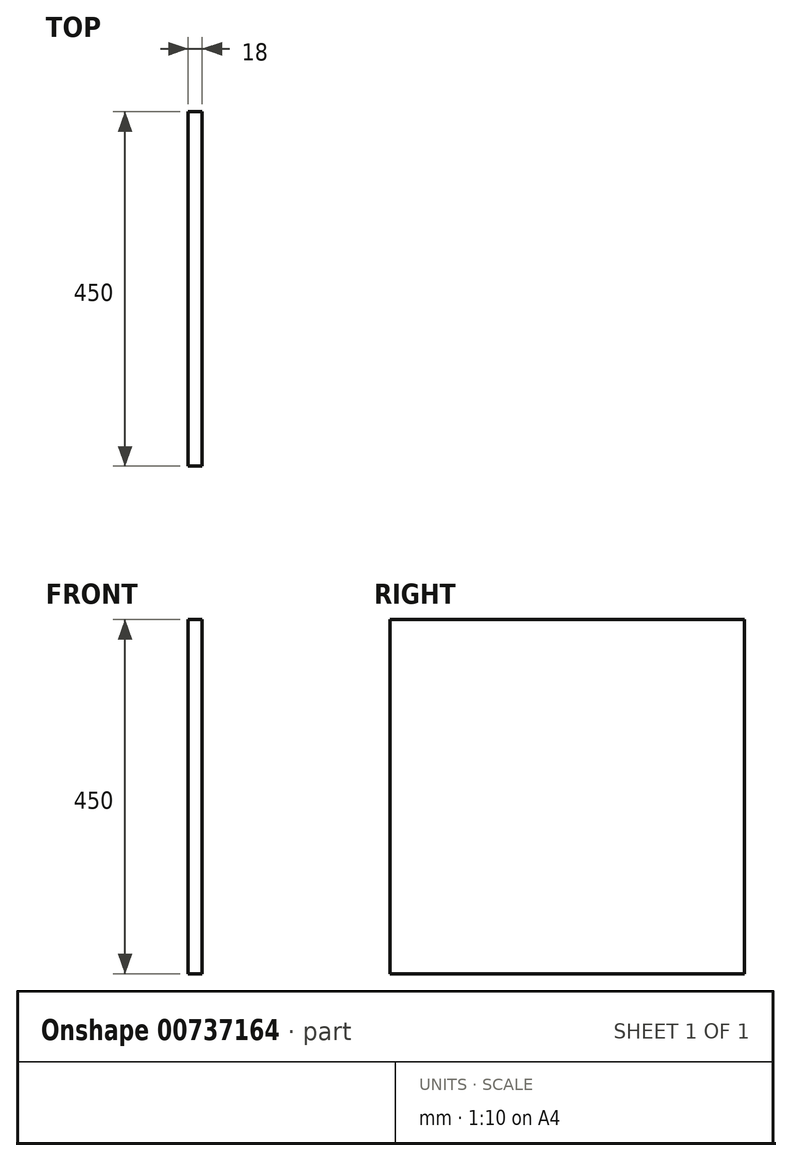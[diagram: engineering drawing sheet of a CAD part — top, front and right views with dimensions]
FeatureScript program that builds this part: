
annotation { "Feature Type Name" : "Feature", "Feature Type Description" : "" }
export const myFeature = defineFeature(function(context is Context, id is Id, definition is map)
    precondition{}
    {
        {
            var Q0;
            Q0=qCreatedBy(makeId("Front.planeOp"),FACE);
            var sketch = newSketch(context, id + "F0", { "sketchPlane" : qUnion([Q0])});
            skLineSegment(sketch, "E0.bottom", {"start": v(9, 225) * mm, "end": v(-9, 225) * mm});
            skLineSegment(sketch, "E0.top", {"start": v(9, -225) * mm, "end": v(-9, -225) * mm});
            skLineSegment(sketch, "E0.left", {"start": v(9, 225) * mm, "end": v(9, -225) * mm});
            skLineSegment(sketch, "E0.right", {"start": v(-9, 225) * mm, "end": v(-9, -225) * mm});
            skPoint(sketch, "E0.middle", {"position": v(0, 0) * mm});
            skSolve(sketch);
        }
        {
            var Q0;
            Q0 = qSketchRegion(id + "F0", true);
            extrude(context, id + "F1", {"entities" : qUnion([Q0]), "endBound" : BoundingType.SYMMETRIC, "depth" : 450 * mm, "offsetDistance" : 25 * mm});
        }
    });
